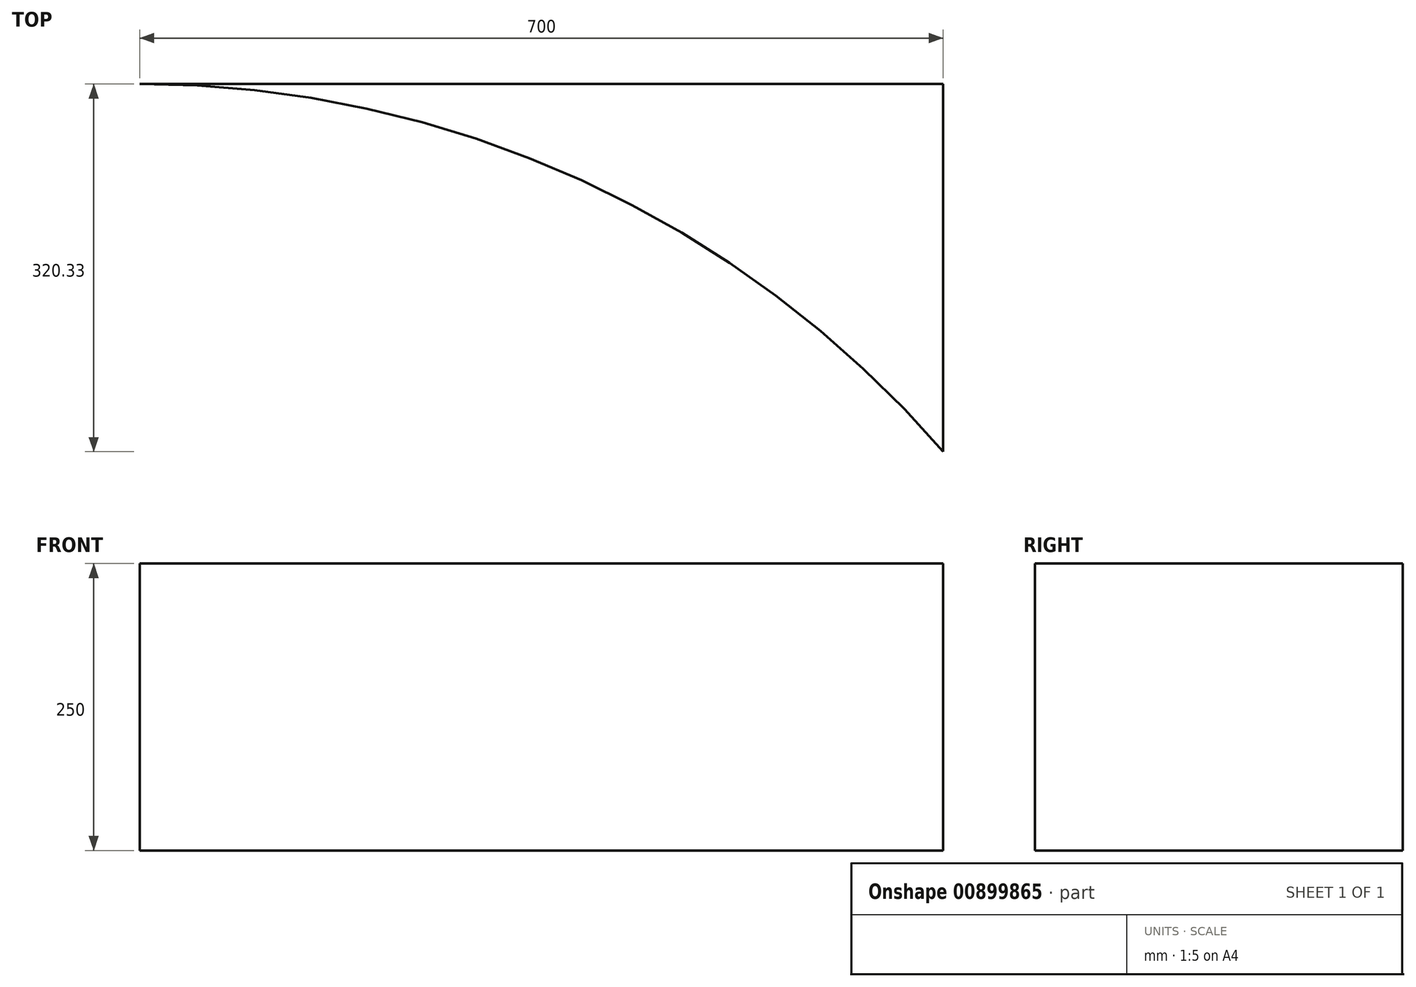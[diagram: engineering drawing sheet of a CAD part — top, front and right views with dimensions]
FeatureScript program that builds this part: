
annotation { "Feature Type Name" : "Feature", "Feature Type Description" : "" }
export const myFeature = defineFeature(function(context is Context, id is Id, definition is map)
    precondition{}
    {
        {
            var Q0;
            Q0=qCreatedBy(makeId("Top.planeOp"),FACE);
            var sketch = newSketch(context, id + "F0", { "sketchPlane" : qUnion([Q0])});
            skLineSegment(sketch, "E0.bottom", {"start": v(0, 0) * mm, "end": v(1400, 0) * mm});
            skLineSegment(sketch, "E0.top", {"start": v(0, 700) * mm, "end": v(1400, 700) * mm});
            skLineSegment(sketch, "E0.left", {"start": v(0, 0) * mm, "end": v(0, 700) * mm});
            skLineSegment(sketch, "E0.right", {"start": v(1400, 0) * mm, "end": v(1400, 700) * mm});
            skSolve(sketch);
        }
        {
            var Q0;
            Q0=makeQuery(id+"F0.imprint","IMPRINT",FACE,{"disambiguationData":[TD([[makeQuery(id+"F0.imprint","IMPRINT",EDGE,{"derivedFrom":sQuery(id+"F0.wireOp",EDGE,"E0.bottom")}),1.0]])]});
            extrude(context, id + "F1", {"entities" : qUnion([Q0]), "depth" : 250 * mm, "offsetDistance" : 25.4 * mm});
        }
        {
            var Q0;
            Q0=makeQuery(id+"F1.opExtrude","CAP_FACE",FACE,{"disambiguationData":[OSD([sQuery(id+"F0.wireOp",EDGE,"E0.bottom"),sQuery(id+"F0.wireOp",EDGE,"E0.top"),sQuery(id+"F0.wireOp",EDGE,"E0.left"),sQuery(id+"F0.wireOp",EDGE,"E0.right")])],"isStart":false});
            var sketch = newSketch(context, id + "F2", { "sketchPlane" : qUnion([Q0])});
            skLineSegment(sketch, "E1", {"start": v(200, 0) * mm, "end": v(200, 300) * mm});
            skLineSegment(sketch, "E2", {"start": v(1200, 0) * mm, "end": v(1200, 300) * mm});
            skArc(sketch, "E3", {"start": v(1200, 300) * mm, "mid": v(700, 500) * mm, "end": v(200, 300) * mm});
            skLineSegment(sketch, "E4", {"start": v(700, 0) * mm, "end": v(700, 700) * mm, "construction": true});
            skSolve(sketch);
        }
        {
            var Q0;
            {var subQ0=sQuery(id+"F2.wireOp",EDGE,"E1");Q0=makeQuery(id+"F2.imprint","IMPRINT",FACE,{"disambiguationData":[TD([[makeQuery(id+"F2.imprint","IMPRINT",EDGE,{"derivedFrom":subQ0}),-1.0]])]});}
            extrude(context, id + "F3", {"entities" : qUnion([Q0]), "operationType" : NewBodyOperationType.REMOVE, "endBound" : BoundingType.THROUGH_ALL, "oppositeDirection" : true, "depth" : 25.4 * mm, "offsetDistance" : 25.4 * mm});
        }
        {
            var Q0;
            Q0=makeQuery(id+"F1.opExtrude","CAP_FACE",FACE,{"disambiguationData":[OSD([sQuery(id+"F0.wireOp",EDGE,"E0.bottom"),sQuery(id+"F0.wireOp",EDGE,"E0.top"),sQuery(id+"F0.wireOp",EDGE,"E0.left"),sQuery(id+"F0.wireOp",EDGE,"E0.right")])],"isStart":false});
            var sketch = newSketch(context, id + "F4", { "sketchPlane" : qUnion([Q0])});
            skArc(sketch, "E5.0", {"start": v(1200, 300) * mm, "mid": v(700, 500) * mm, "end": v(200, 300) * mm, "construction": true});
            skArc(sketch, "E6", {"start": v(700, 700) * mm, "mid": v(1084.9, 616.11) * mm, "end": v(1400, 379.67) * mm});
            skLineSegment(sketch, "E7", {"start": v(700, 700) * mm, "end": v(700, -225) * mm, "construction": true});
            skArc(sketch, "E8.MirrorCS", {"start": v(700, 700) * mm, "mid": v(315.1, 616.11) * mm, "end": v(0, 379.67) * mm});
            skSolve(sketch);
        }
        {
            var Q0;
            {var subQ0=sQuery(id+"F4.wireOp",EDGE,"E8.MirrorCS");Q0=makeQuery(id+"F4.imprint","IMPRINT",FACE,{"disambiguationData":[TD([[makeQuery(id+"F4.imprint","IMPRINT",EDGE,{"derivedFrom":subQ0}),-1.0]])]});}
            var Q1;
            {var subQ0=sQuery(id+"F4.wireOp",EDGE,"E6");Q1=makeQuery(id+"F4.imprint","IMPRINT",FACE,{"disambiguationData":[TD([[makeQuery(id+"F4.imprint","IMPRINT",EDGE,{"derivedFrom":subQ0}),1.0]])]});}
            extrude(context, id + "F5", {"entities" : qUnion([Q0, Q1]), "operationType" : NewBodyOperationType.REMOVE, "endBound" : BoundingType.THROUGH_ALL, "oppositeDirection" : true, "depth" : 25.4 * mm, "offsetDistance" : 25.4 * mm});
        }
    });
